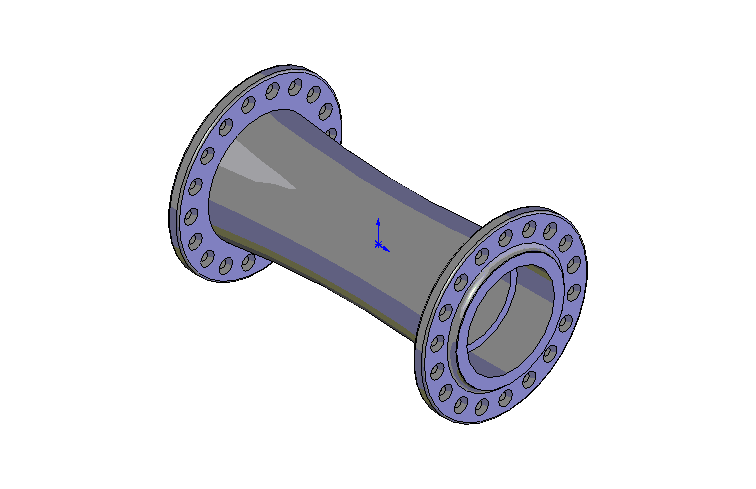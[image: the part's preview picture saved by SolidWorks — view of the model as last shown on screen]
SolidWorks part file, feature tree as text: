
SOLIDWORKS PART (.sldprt)
format: sldprt  version: not decoded by parser v0  size: 518,144 bytes
history: native  units: mm
features: sketch x4, plane x3, cut_extrude x2, material x1, revolve x1, fillet x1, chamfer x1, pattern_circular x1, cut_revolve x1 (+10 scaffold rows collapsed)
feature tree (25):
  scaffold x10  (default folders/planes/origin — collapsed)
  material  "Matériau <non spécifié>"
  plane  "Plan de face"
  plane  "Plan de dessus"
  plane  "Plan de droite"
  sketch  "Esquisse1"  dims[c1.D6=~31.37397mm c1.D9=270.0mm c1.D2=273.0mm c2.D6=1.3mm c2.D1=3.0mm c2.D2=27.0mm c2.D3=32.0mm c2.D4=49.0mm c2.D5=31.0mm c3.D6=3.0mm c3.D7=78.5mm c3.D8=75.5mm c3.D9=26.5mm c3.D2=3.0mm c3.D10=22.0mm]
  revolve  "Révolution1"  Angle=360deg
  fillet  "Congé1"  Radius=0.5mm
  sketch  "Esquisse2"  dims[D1=2.0mm D2=41.0mm]
  cut_extrude  "Enlèv. mat.-Extru.1"  [1 undecoded]
  sketch  "Esquisse3"  dims[c1.D1=53.9mm c2.D1=10.0deg]
  cut_extrude  "Enlèv. mat.-Extru.2"  [1 undecoded]
  chamfer  "Chanfrein1"  Distance=1mm Angle=45deg
  pattern_circular  "Répétition circulaire1"  Count=18 Angle=20deg
  sketch  "Esquisse4"  dims[c1.D1=26.0mm c1.D2=11.0mm c1.D3=22.0mm c2.D1=26.0mm]
  cut_revolve  "Enlèvement de matière-Révolution3"  Angle=360deg
decode coverage: 9 of 11 modeling features carry decoded parameters
note: ~ marks probable driven/reference dimensions
note: 2 parameter values undecoded
note: suppression state not decoded; provenance and decode notes live in map.json
